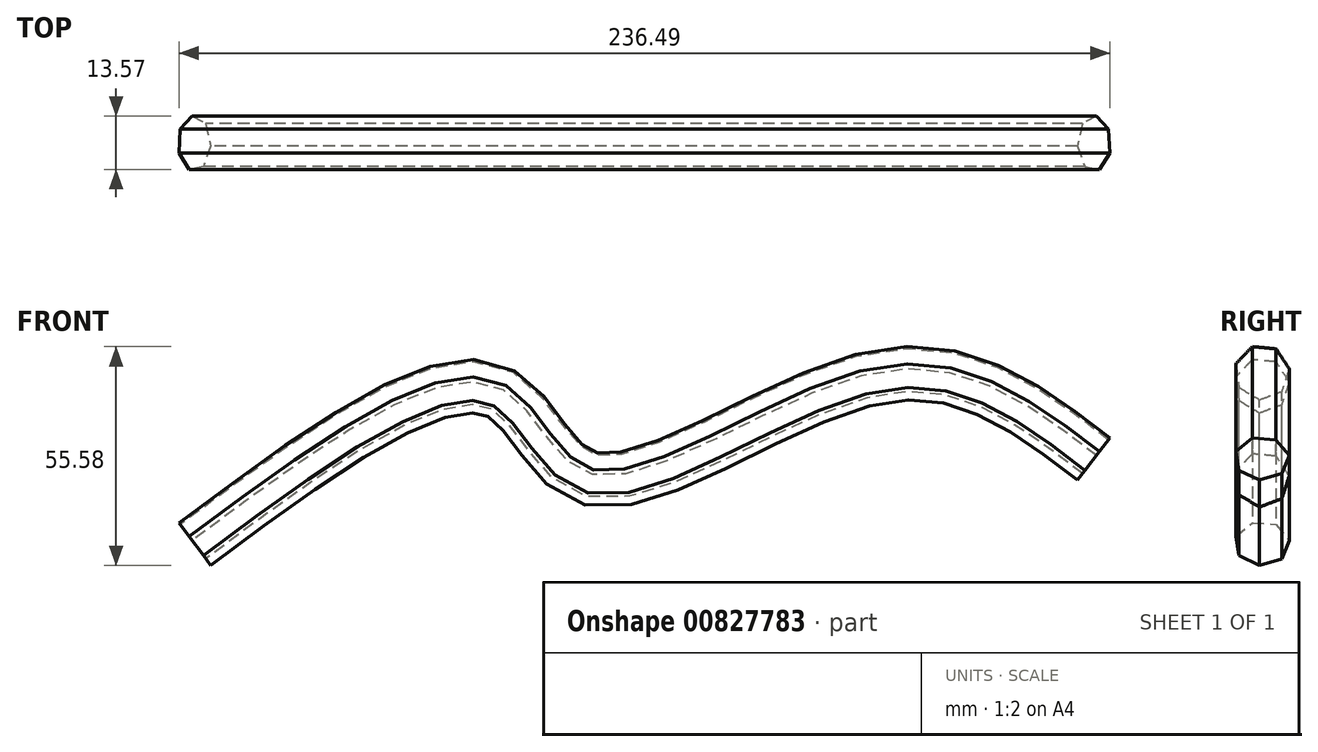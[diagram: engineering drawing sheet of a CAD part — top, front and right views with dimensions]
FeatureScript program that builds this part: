
annotation { "Feature Type Name" : "Feature", "Feature Type Description" : "" }
export const myFeature = defineFeature(function(context is Context, id is Id, definition is map)
    precondition{}
    {
        {
            var Q0;
            Q0=qCreatedBy(makeId("Front.planeOp"),FACE);
            var sketch = newSketch(context, id + "F0", { "sketchPlane" : qUnion([Q0])});
            skFitSpline(sketch, "E0", {"points": [v(-125.37, 7.17) * mm, v(-48.51, 46.14) * mm, v(-24.66, 23.87) * mm, v(49.54, 50) * mm, v(103.43, 28.75) * mm], "startDerivative": vector(312.1, 232.54) * mm, "endDerivative": vector(200.17, -154.52) * mm});
            skSolve(sketch);
        }
        {
            var Q0;
            Q0=sQuery(id+"F0.wireOp",EDGE,"E0");
            var Q1;
            Q1=sQuery(id+"F0.wireOp",VERTEX,"E0.end");
            cPlane(context, id + "F1", {"entities" : qUnion([Q0, Q1]), "cplaneType" : CPlaneType.CURVE_POINT, "offset" : 25.4 * mm, "width" : 152.4 * mm, "height" : 152.4 * mm});
        }
        {
            var Q0;
            Q0=qCreatedBy(id+"F1.planeOp",FACE);
            var sketch = newSketch(context, id + "F2", { "sketchPlane" : qUnion([Q0])});
            skCircle(sketch, "E1.cCircle", {"center": v(0, 85.78) * mm, "radius": 6.3 * mm, "construction": true});
            skLineSegment(sketch, "E1.0", {"start": v(3.6, 91.77) * mm, "end": v(6.93, 86.7) * mm});
            skLineSegment(sketch, "E1.1", {"start": v(6.93, 86.7) * mm, "end": v(5.04, 80.94) * mm});
            skLineSegment(sketch, "E1.2", {"start": v(5.04, 80.94) * mm, "end": v(-0.65, 78.82) * mm});
            skLineSegment(sketch, "E1.3", {"start": v(-0.65, 78.82) * mm, "end": v(-5.84, 81.95) * mm});
            skLineSegment(sketch, "E1.4", {"start": v(-5.84, 81.95) * mm, "end": v(-6.64, 87.96) * mm});
            skLineSegment(sketch, "E1.5", {"start": v(-6.64, 87.96) * mm, "end": v(-2.44, 92.33) * mm});
            skLineSegment(sketch, "E1.6", {"start": v(-2.44, 92.33) * mm, "end": v(3.6, 91.77) * mm});
            skPoint(sketch, "E1.0.midPoint", {"position": v(5.26, 89.23) * mm});
            skSolve(sketch);
        }
        {
            var Q0;
            Q0 = qSketchRegion(id + "F2", true);
            var Q1;
            Q1=sQuery(id+"F0.wireOp",EDGE,"E0");
            sweep(context, id + "F3", {"profiles" : qUnion([Q0]), "path" : qUnion([Q1])});
        }
    });
